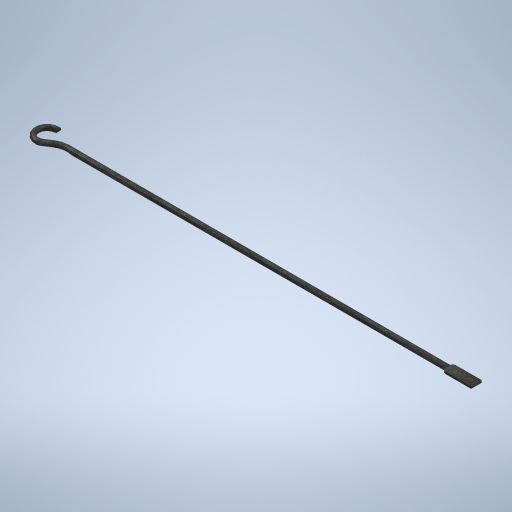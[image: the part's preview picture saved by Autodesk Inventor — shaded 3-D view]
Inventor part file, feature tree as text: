
AUTODESK INVENTOR PART (.ipt)
format: ipt  version: 2024 (Build 280153000, 153)  size: 369,664 bytes
history: native  units: mm
features: extrude x2, other x2, fillet x2, sketch x2
ambient origin geometry x8: Origin, YZ Plane, XZ Plane, XY Plane, X Axis, Y Axis, Z Axis, Center Point
bodies: Solid1 (feature_tree)
feature tree (8):
  extrude  "Extrusion1"  Depth=35.0mm
  other  "Full Round Fillet1"
  other  "Full Round Fillet4"
  extrude  "Extrusion3"  Depth=2.0mm
  fillet  "Fillet2"  Radius=12.5mm
  fillet  "Fillet3"  Radius=8.0mm
  sketch  "Sketch1"  dims[d0=725.0mm d2=35.0mm]
  sketch  "Sketch3"  dims[d3=12.5mm d4=35.0mm d6=12.5mm d7=8.0mm d8=8.0mm d9=8.0mm d10=8.0mm d11=0.0mm d18=5.0mm d19=5.0mm d20=50.0mm d21=5.0mm d22=5.0mm d23=2.0mm d24=2.0mm d25=50.0mm d26=0.0mm d27=2.0mm d28=2.0mm]
